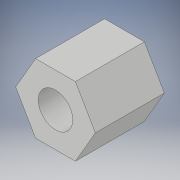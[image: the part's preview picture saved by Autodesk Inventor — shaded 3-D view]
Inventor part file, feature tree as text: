
AUTODESK INVENTOR PART (.ipt)
format: ipt  version: 2018 (Build 220112000, 112)  size: 97,280 bytes
history: native  units: in
note: dims shown in document units (in); Inventor stores cm internally (conversion verified against a paired STEP export)
features: extrude x1, sketch x1
ambient origin geometry x8: Origin, YZ Plane, XZ Plane, XY Plane, X Axis, Y Axis, Z Axis, Center Point
bodies: Solid1 (feature_tree)
feature tree (2):
  extrude  "Extrusion1"  Depth=0.5in
  sketch  "Sketch1"  dims[d0=0.5in d1=0.25in d2=0.5in d3=0.0in]
